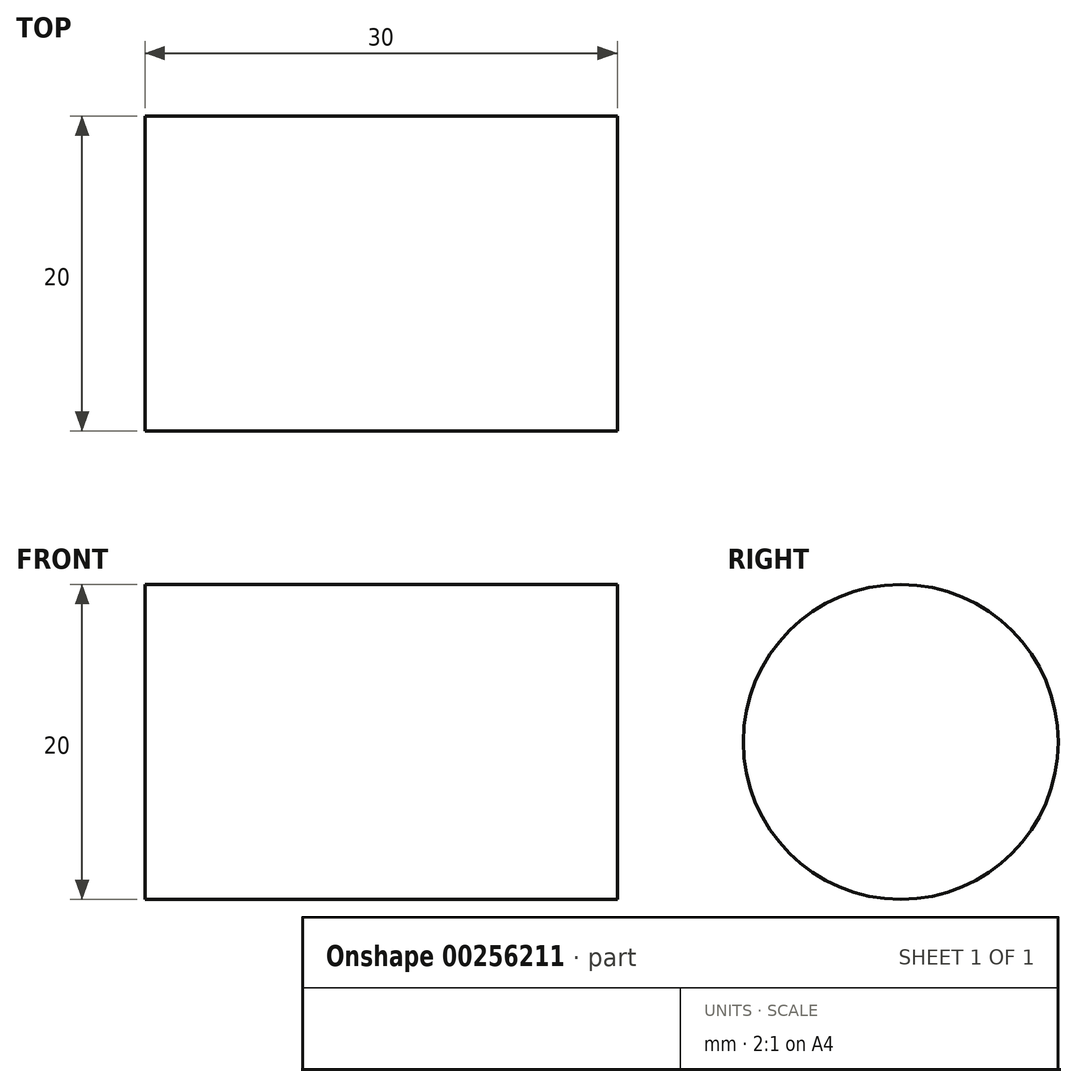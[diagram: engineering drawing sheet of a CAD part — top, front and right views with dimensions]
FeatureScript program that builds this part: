
annotation { "Feature Type Name" : "Feature", "Feature Type Description" : "" }
export const myFeature = defineFeature(function(context is Context, id is Id, definition is map)
    precondition{}
    {
        {
            var Q0;
            Q0=qCreatedBy(makeId("Right.planeOp"),FACE);
            var sketch = newSketch(context, id + "F0", { "sketchPlane" : qUnion([Q0])});
            skCircle(sketch, "E0", {"center": v(0, 0) * mm, "radius": 10 * mm});
            skSolve(sketch);
        }
        {
            var Q0;
            Q0=sQuery(id+"F0.wireOp",EDGE,"E0");
            extrude(context, id + "F1", {"bodyType" : ToolBodyType.SURFACE, "surfaceEntities" : qUnion([Q0]), "depth" : 30 * mm});
        }
    });
